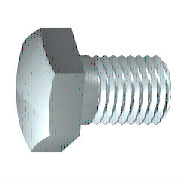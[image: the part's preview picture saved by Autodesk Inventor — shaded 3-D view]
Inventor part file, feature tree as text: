
AUTODESK INVENTOR PART (.ipt)
format: ipt  version: 2021 (Build 250183000, 183)  size: 194,048 bytes
history: native  units: mm (DEFAULTED — no unit token found)
features: sketch x3, extrude x1, chamfer x1, plane x1
ambient origin geometry x7: Origin, YZ Plane, XZ Plane, X Axis, Y Axis, Z Axis, Center Point
bodies: Solid1 (feature_tree), Body (feature_tree)
feature tree (6):
  extrude  "Head"  Depth=34.0mm
  chamfer  "Chamfer1"  Distance=8.2mm
  plane  "Work Plane1"
  sketch  "Sketch1"  dims[d0=40.0mm d1=34.0mm]
  sketch  "Sketch2"  dims[d2=14.0mm]
  sketch  "Sketch4"  dims[d12=90.0deg d3=8.2mm d4=0.0mm d5=30.0deg d21=90.0deg d6=1.2269mm d7=1.227mm d8=0.0mm d9=0.6001mm d10=19.37mm d11=21.0mm d13=1.227mm d14=14.0mm d15=34.0mm d16=0.0mm d19=21.0mm d55=45.0deg d57=0.0mm d58=0.0mm]
